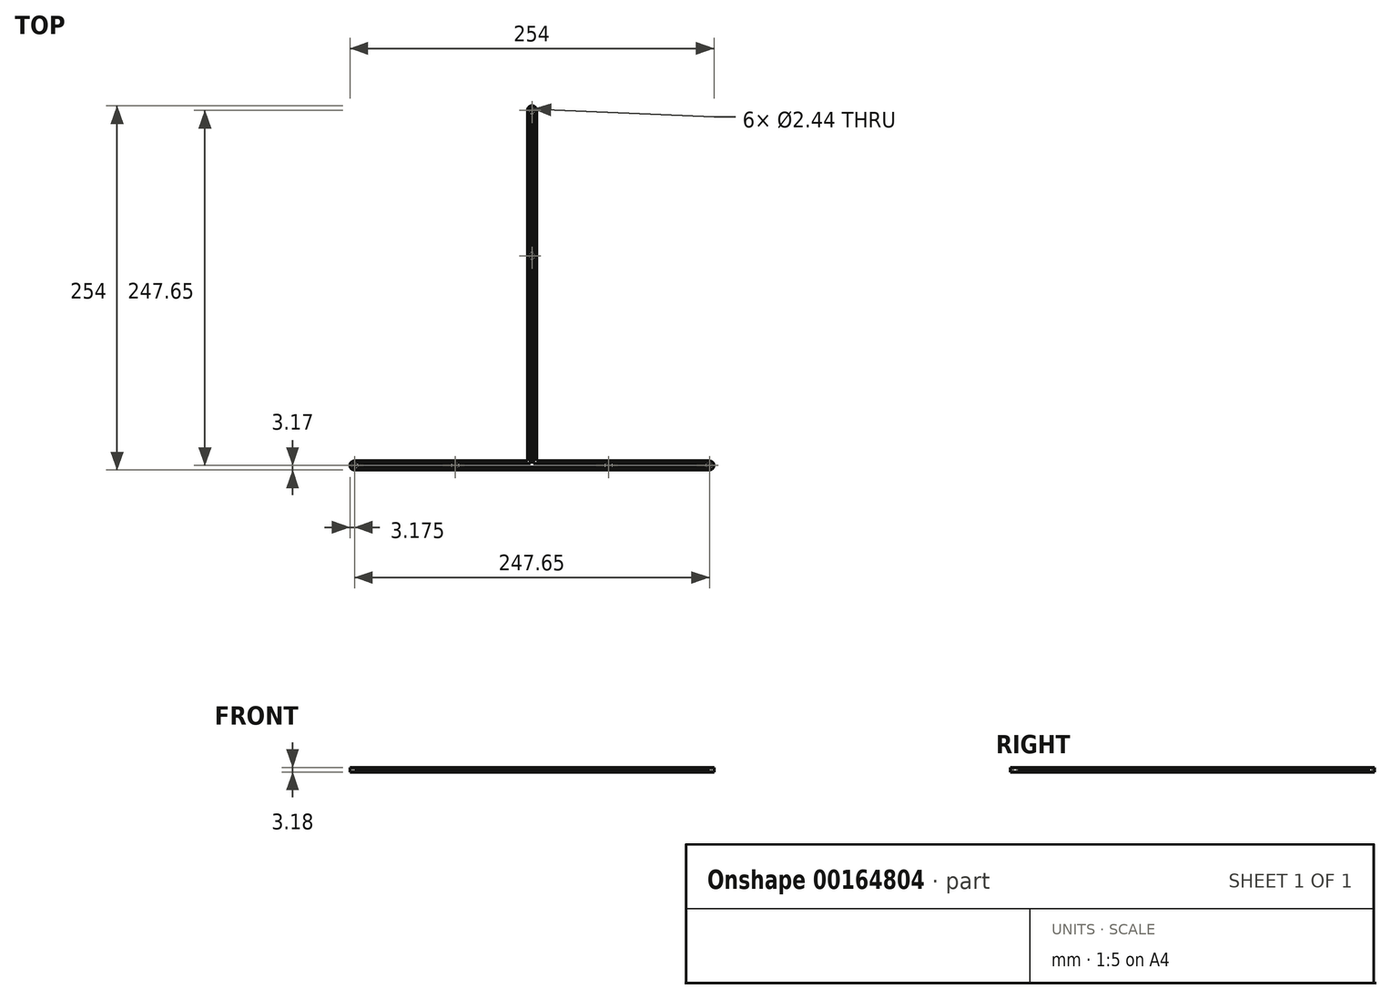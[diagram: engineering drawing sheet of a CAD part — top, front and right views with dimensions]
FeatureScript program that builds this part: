
annotation { "Feature Type Name" : "Feature", "Feature Type Description" : "" }
export const myFeature = defineFeature(function(context is Context, id is Id, definition is map)
    precondition{}
    {
        {
            var Q0;
            Q0=qCreatedBy(makeId("Top.planeOp"),FACE);
            var sketch = newSketch(context, id + "F0", { "sketchPlane" : qUnion([Q0])});
            skLineSegment(sketch, "E0", {"start": v(-123.83, 0) * mm, "end": v(-53.52, 0) * mm, "construction": true});
            skLineSegment(sketch, "E1", {"start": v(-53.52, 0) * mm, "end": v(53.52, 0) * mm, "construction": true});
            skLineSegment(sketch, "E2", {"start": v(53.52, 0) * mm, "end": v(123.83, 0) * mm, "construction": true});
            skCircle(sketch, "E3", {"center": v(-123.83, 0) * mm, "radius": 1.22 * mm});
            skCircle(sketch, "E4", {"center": v(-53.52, 0) * mm, "radius": 1.22 * mm});
            skCircle(sketch, "E5", {"center": v(53.52, 0) * mm, "radius": 1.22 * mm});
            skCircle(sketch, "E6", {"center": v(123.83, 0) * mm, "radius": 1.22 * mm});
            skLineSegment(sketch, "E7", {"start": v(0, 0) * mm, "end": v(0, 146.05) * mm, "construction": true});
            skLineSegment(sketch, "E8", {"start": v(0, 146.05) * mm, "end": v(0, 247.65) * mm, "construction": true});
            skCircle(sketch, "E9", {"center": v(0, 247.65) * mm, "radius": 1.22 * mm});
            skCircle(sketch, "E10", {"center": v(0, 146.05) * mm, "radius": 1.22 * mm});
            skLineSegment(sketch, "E11", {"start": v(-123.83, 0) * mm, "end": v(-127, 0) * mm, "construction": true});
            skLineSegment(sketch, "E12", {"start": v(123.83, 0) * mm, "end": v(127, 0) * mm, "construction": true});
            skLineSegment(sketch, "E13", {"start": v(0, 247.65) * mm, "end": v(0, 250.83) * mm, "construction": true});
            skLineSegment(sketch, "E14", {"start": v(-123.83, 0) * mm, "end": v(-123.83, -3.18) * mm, "construction": true});
            skLineSegment(sketch, "E15.bottom", {"start": v(-127, -3.18) * mm, "end": v(127, -3.18) * mm});
            skLineSegment(sketch, "E15.top", {"start": v(-127, 3.18) * mm, "end": v(-3.17, 3.18) * mm});
            skLineSegment(sketch, "E15.left", {"start": v(-127, -3.18) * mm, "end": v(-127, 3.18) * mm});
            skLineSegment(sketch, "E16.top", {"start": v(127, 3.18) * mm, "end": v(3.18, 3.18) * mm});
            skLineSegment(sketch, "E16.left", {"start": v(127, -3.18) * mm, "end": v(127, 3.18) * mm});
            skLineSegment(sketch, "E17.bottom", {"start": v(-3.17, 250.83) * mm, "end": v(3.17, 250.83) * mm});
            skLineSegment(sketch, "E17.left", {"start": v(-3.17, 250.83) * mm, "end": v(-3.17, 3.18) * mm});
            skLineSegment(sketch, "E17.right", {"start": v(3.18, 250.83) * mm, "end": v(3.18, 3.18) * mm});
            skLineSegment(sketch, "E18", {"start": v(-88.67, 0) * mm, "end": v(-88.67, -177.34) * mm, "construction": true});
            skLineSegment(sketch, "E19", {"start": v(-88.67, -177.34) * mm, "end": v(88.67, -177.34) * mm, "construction": true});
            skLineSegment(sketch, "E20", {"start": v(88.67, -177.34) * mm, "end": v(88.67, 0) * mm, "construction": true});
            skSolve(sketch);
        }
        {
            var Q0;
            Q0=makeQuery(id+"F0.imprint","IMPRINT",FACE,{"disambiguationData":[TD([[makeQuery(id+"F0.imprint","IMPRINT",EDGE,{"derivedFrom":sQuery(id+"F0.wireOp",EDGE,"E3")}),-1.0]])]});
            extrude(context, id + "F1", {"entities" : qUnion([Q0]), "depth" : 1.59 * mm});
        }
        {
            var Q0;
            Q0=makeQuery(id+"F1.opExtrude","SWEPT_EDGE",EDGE,{"disambiguationData":[OSD([sQuery(id+"F0.wireOp",EDGE,"E15.bottom"),sQuery(id+"F0.wireOp",EDGE,"E15.left")])]});
            var Q1;
            Q1=makeQuery(id+"F1.opExtrude","SWEPT_EDGE",EDGE,{"disambiguationData":[OSD([sQuery(id+"F0.wireOp",EDGE,"E15.top"),sQuery(id+"F0.wireOp",EDGE,"E15.left")])]});
            var Q2;
            Q2=makeQuery(id+"F1.opExtrude","SWEPT_EDGE",EDGE,{"disambiguationData":[OSD([sQuery(id+"F0.wireOp",EDGE,"E16.top"),sQuery(id+"F0.wireOp",EDGE,"E16.left")])]});
            var Q3;
            Q3=makeQuery(id+"F1.opExtrude","SWEPT_EDGE",EDGE,{"disambiguationData":[OSD([sQuery(id+"F0.wireOp",EDGE,"E15.bottom"),sQuery(id+"F0.wireOp",EDGE,"E16.left")])]});
            var Q4;
            Q4=makeQuery(id+"F1.opExtrude","SWEPT_EDGE",EDGE,{"disambiguationData":[OSD([sQuery(id+"F0.wireOp",EDGE,"E17.bottom"),sQuery(id+"F0.wireOp",EDGE,"E17.left")])]});
            var Q5;
            Q5=makeQuery(id+"F1.opExtrude","SWEPT_EDGE",EDGE,{"disambiguationData":[OSD([sQuery(id+"F0.wireOp",EDGE,"E17.bottom"),sQuery(id+"F0.wireOp",EDGE,"E17.right")])]});
            fillet(context, id + "F2", {"entities" : qUnion([Q0, Q1, Q2, Q3, Q4, Q5]), "radius" : 3.17 * mm, "tangentPropagation" : true, "allowEdgeOverflow" : false});
        }
        {
            var Q0;
            Q0=makeQuery(id+"F1.opExtrude","CAP_FACE",FACE,{"disambiguationData":[OSD([sQuery(id+"F0.wireOp",EDGE,"E3"),sQuery(id+"F0.wireOp",EDGE,"E4"),sQuery(id+"F0.wireOp",EDGE,"E5"),sQuery(id+"F0.wireOp",EDGE,"E6"),sQuery(id+"F0.wireOp",EDGE,"E9"),sQuery(id+"F0.wireOp",EDGE,"E10"),sQuery(id+"F0.wireOp",EDGE,"E15.bottom"),sQuery(id+"F0.wireOp",EDGE,"E15.top"),sQuery(id+"F0.wireOp",EDGE,"E15.left"),sQuery(id+"F0.wireOp",EDGE,"E16.top"),sQuery(id+"F0.wireOp",EDGE,"E16.left"),sQuery(id+"F0.wireOp",EDGE,"E17.bottom"),sQuery(id+"F0.wireOp",EDGE,"E17.left"),sQuery(id+"F0.wireOp",EDGE,"E17.right")])],"isStart":false});
            var sketch = newSketch(context, id + "F3", { "sketchPlane" : qUnion([Q0])});
            skArc(sketch, "E21", {"start": v(-120.88, 1.2) * mm, "mid": v(-127, 0) * mm, "end": v(-120.88, -1.2) * mm});
            skLineSegment(sketch, "E22", {"start": v(-123.83, 0) * mm, "end": v(-120.88, 0) * mm, "construction": true});
            skCircle(sketch, "E23", {"center": v(-123.83, 0) * mm, "radius": 1.22 * mm});
            skLineSegment(sketch, "E24.bottom", {"start": v(-120.88, 1.2) * mm, "end": v(-56.46, 1.2) * mm});
            skLineSegment(sketch, "E24.top", {"start": v(-120.88, -1.2) * mm, "end": v(-56.46, -1.2) * mm});
            skLineSegment(sketch, "E24.left", {"start": v(-120.88, 1.2) * mm, "end": v(-120.88, -1.2) * mm, "construction": true});
            skLineSegment(sketch, "E24.right", {"start": v(-56.46, 1.2) * mm, "end": v(-56.46, -1.2) * mm, "construction": true});
            skArc(sketch, "E25", {"start": v(-50.57, 1.2) * mm, "mid": v(-53.52, 3.17) * mm, "end": v(-56.46, 1.2) * mm});
            skArc(sketch, "E26", {"start": v(-56.46, -1.2) * mm, "mid": v(-53.52, -3.18) * mm, "end": v(-50.57, -1.2) * mm});
            skLineSegment(sketch, "E27.top", {"start": v(-1.2, 143.1) * mm, "end": v(1.2, 143.1) * mm, "construction": true});
            skLineSegment(sketch, "E27.left", {"start": v(-1.2, 1.2) * mm, "end": v(-1.2, 143.1) * mm});
            skLineSegment(sketch, "E27.right", {"start": v(1.2, 1.2) * mm, "end": v(1.2, 143.1) * mm});
            skLineSegment(sketch, "E28.bottom", {"start": v(-50.57, 1.2) * mm, "end": v(-1.2, 1.2) * mm});
            skLineSegment(sketch, "E28.top", {"start": v(-50.57, -1.2) * mm, "end": v(50.57, -1.2) * mm});
            skLineSegment(sketch, "E28.left", {"start": v(-50.57, 1.2) * mm, "end": v(-50.57, -1.2) * mm, "construction": true});
            skLineSegment(sketch, "E29", {"start": v(0, -3.18) * mm, "end": v(0, -1.2) * mm, "construction": true});
            skLineSegment(sketch, "E30", {"start": v(1.2, 1.2) * mm, "end": v(50.57, 1.2) * mm});
            skArc(sketch, "E31", {"start": v(50.57, -1.2) * mm, "mid": v(53.52, -3.18) * mm, "end": v(56.46, -1.2) * mm});
            skArc(sketch, "E32", {"start": v(56.46, 1.2) * mm, "mid": v(53.52, 3.17) * mm, "end": v(50.57, 1.2) * mm});
            skLineSegment(sketch, "E33", {"start": v(0, -1.2) * mm, "end": v(0, 143.1) * mm, "construction": true});
            skArc(sketch, "E34", {"start": v(1.2, 244.7) * mm, "mid": v(0, 250.82) * mm, "end": v(-1.2, 244.7) * mm});
            skLineSegment(sketch, "E35.bottom", {"start": v(-1.2, 244.7) * mm, "end": v(1.2, 244.7) * mm, "construction": true});
            skLineSegment(sketch, "E35.top", {"start": v(-1.2, 149) * mm, "end": v(1.2, 149) * mm, "construction": true});
            skLineSegment(sketch, "E35.left", {"start": v(-1.2, 244.7) * mm, "end": v(-1.2, 149) * mm});
            skLineSegment(sketch, "E35.right", {"start": v(1.2, 244.7) * mm, "end": v(1.2, 149) * mm});
            skArc(sketch, "E36", {"start": v(-1.2, 149) * mm, "mid": v(-3.17, 146.05) * mm, "end": v(-1.2, 143.1) * mm});
            skArc(sketch, "E37", {"start": v(1.2, 143.1) * mm, "mid": v(3.17, 146.05) * mm, "end": v(1.2, 149) * mm});
            skLineSegment(sketch, "E38.bottom", {"start": v(56.46, 1.2) * mm, "end": v(120.88, 1.2) * mm});
            skLineSegment(sketch, "E38.top", {"start": v(56.46, -1.2) * mm, "end": v(120.88, -1.2) * mm});
            skLineSegment(sketch, "E38.left", {"start": v(56.46, 1.2) * mm, "end": v(56.46, -1.2) * mm, "construction": true});
            skLineSegment(sketch, "E38.right", {"start": v(120.88, 1.2) * mm, "end": v(120.88, -1.2) * mm, "construction": true});
            skArc(sketch, "E39", {"start": v(120.88, -1.2) * mm, "mid": v(127, 0) * mm, "end": v(120.88, 1.2) * mm});
            skCircle(sketch, "E40", {"center": v(0, 247.65) * mm, "radius": 1.22 * mm});
            skCircle(sketch, "E41", {"center": v(53.52, 0) * mm, "radius": 1.22 * mm});
            skCircle(sketch, "E42", {"center": v(0, 146.05) * mm, "radius": 1.22 * mm});
            skCircle(sketch, "E43", {"center": v(-53.52, 0) * mm, "radius": 1.22 * mm});
            skCircle(sketch, "E44", {"center": v(123.83, 0) * mm, "radius": 1.22 * mm});
            skSolve(sketch);
        }
        {
            var Q0;
            Q0 = qSketchRegion(id + "F3", true);
            extrude(context, id + "F4", {"entities" : qUnion([Q0]), "operationType" : NewBodyOperationType.ADD, "depth" : 1.59 * mm});
        }
    });
